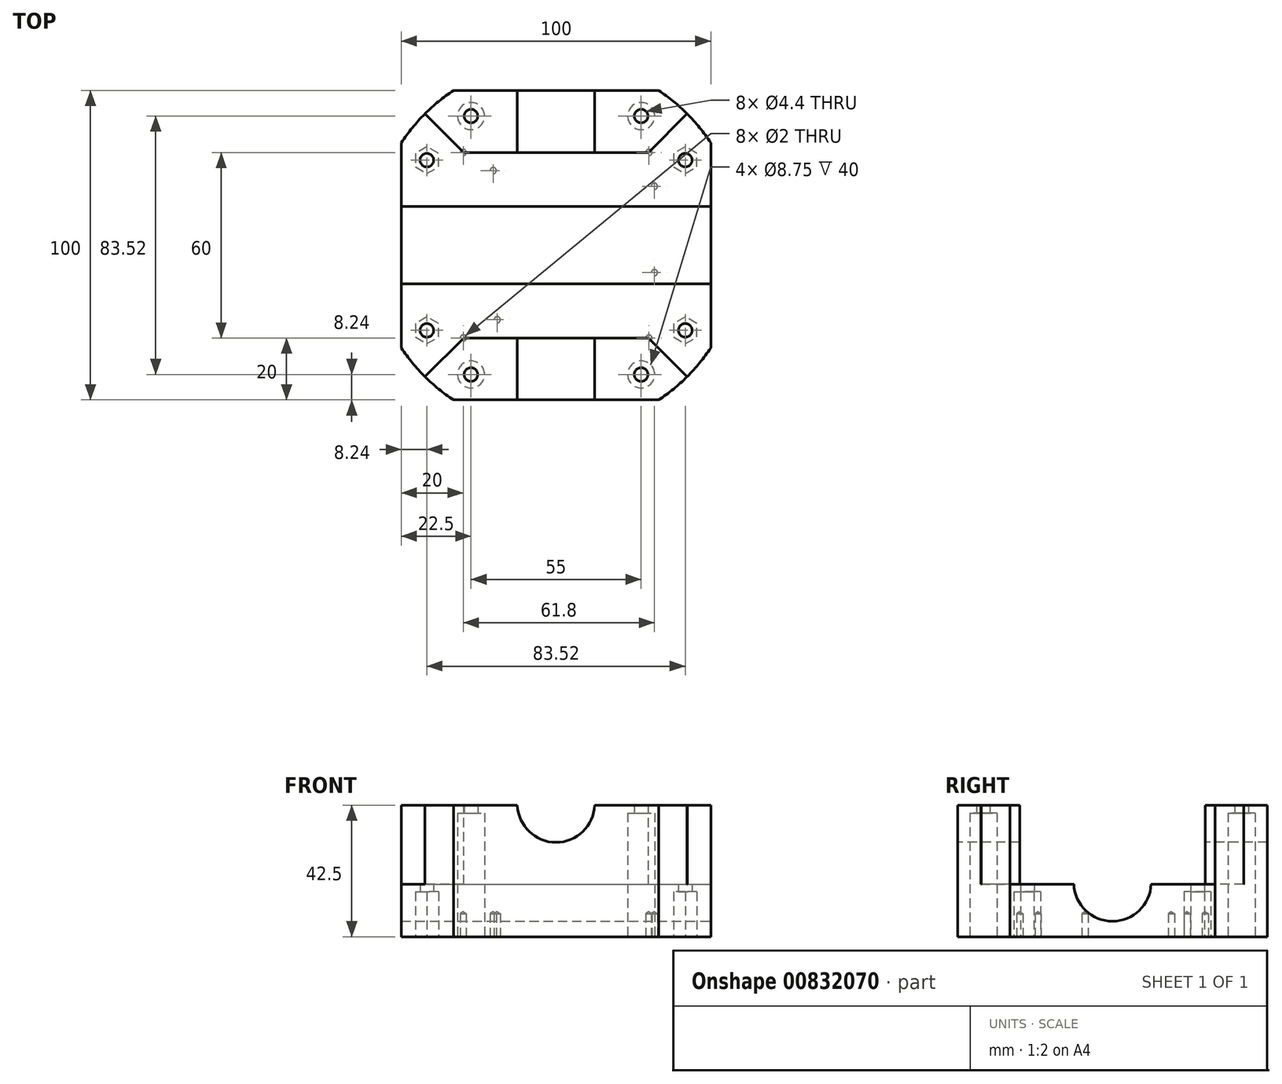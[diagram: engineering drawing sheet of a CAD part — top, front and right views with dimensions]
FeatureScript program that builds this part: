
annotation { "Feature Type Name" : "Feature", "Feature Type Description" : "" }
export const myFeature = defineFeature(function(context is Context, id is Id, definition is map)
    precondition{}
    {
        {
            var Q0;
            Q0=qCreatedBy(makeId("Top.planeOp"),FACE);
            var sketch = newSketch(context, id + "F0", { "sketchPlane" : qUnion([Q0])});
            skLineSegment(sketch, "E0.bottom", {"start": v(-33.17, 50) * mm, "end": v(33.17, 50) * mm});
            skLineSegment(sketch, "E0.top", {"start": v(-33.17, -50) * mm, "end": v(33.17, -50) * mm});
            skLineSegment(sketch, "E0.left", {"start": v(-50, 33.17) * mm, "end": v(-50, -33.17) * mm});
            skLineSegment(sketch, "E0.right", {"start": v(50, 33.17) * mm, "end": v(50, -33.17) * mm});
            skArc(sketch, "E1", {"start": v(-50, -33.17) * mm, "mid": v(-42.43, -42.43) * mm, "end": v(-33.17, -50) * mm});
            skArc(sketch, "E2.trimOffspring", {"start": v(33.17, -50) * mm, "mid": v(42.43, -42.43) * mm, "end": v(50, -33.17) * mm});
            skArc(sketch, "E3.trimOffspring", {"start": v(50, 33.17) * mm, "mid": v(42.43, 42.43) * mm, "end": v(33.17, 50) * mm});
            skArc(sketch, "E4.trimOffspring", {"start": v(-33.17, 50) * mm, "mid": v(-42.43, 42.43) * mm, "end": v(-50, 33.17) * mm});
            skSolve(sketch);
        }
        {
            var Q0;
            Q0=makeQuery(id+"F0.imprint","IMPRINT",FACE,{"disambiguationData":[TD([[makeQuery(id+"F0.imprint","IMPRINT",EDGE,{"derivedFrom":sQuery(id+"F0.wireOp",EDGE,"E0.bottom")}),-1.0]])]});
            extrude(context, id + "F1", {"entities" : qUnion([Q0]), "depth" : (17.5 + 25) * mm, "offsetDistance" : 25 * mm});
        }
        {
            var Q0;
            Q0=makeQuery(id+"F1.opExtrude","CAP_FACE",FACE,{"disambiguationData":[OSD([sQuery(id+"F0.wireOp",EDGE,"E0.bottom"),sQuery(id+"F0.wireOp",EDGE,"E0.top"),sQuery(id+"F0.wireOp",EDGE,"E0.left"),sQuery(id+"F0.wireOp",EDGE,"E0.right"),sQuery(id+"F0.wireOp",EDGE,"E1"),sQuery(id+"F0.wireOp",EDGE,"E2.trimOffspring"),sQuery(id+"F0.wireOp",EDGE,"E3.trimOffspring"),sQuery(id+"F0.wireOp",EDGE,"E4.trimOffspring")])],"isStart":false});
            var sketch = newSketch(context, id + "F2", { "sketchPlane" : qUnion([Q0])});
            skLineSegment(sketch, "E5", {"start": v(-42.43, 42.43) * mm, "end": v(-30, 30) * mm, "construction": true});
            skLineSegment(sketch, "E6", {"start": v(42.43, 42.43) * mm, "end": v(30, 30) * mm, "construction": true});
            skLineSegment(sketch, "E7.bottom", {"start": v(-30, 30) * mm, "end": v(-29.86, 30) * mm, "construction": true});
            skLineSegment(sketch, "E7.top", {"start": v(-30, -30) * mm, "end": v(-29.86, -30) * mm, "construction": true});
            skLineSegment(sketch, "E8.trimOffspring", {"start": v(30, -30) * mm, "end": v(42.43, -42.43) * mm, "construction": true});
            skLineSegment(sketch, "E9.trimOffspring", {"start": v(-30, -30) * mm, "end": v(-42.43, -42.43) * mm, "construction": true});
            skArc(sketch, "E10.0", {"start": v(-33.17, 50) * mm, "mid": v(-42.43, 42.43) * mm, "end": v(-50, 33.17) * mm});
            skArc(sketch, "E11.0.0", {"start": v(-50, -33.17) * mm, "mid": v(-42.43, -42.43) * mm, "end": v(-33.17, -50) * mm});
            skLineSegment(sketch, "E11.0.1", {"start": v(-33.17, -50) * mm, "end": v(33.17, -50) * mm});
            skArc(sketch, "E11.0.2", {"start": v(33.17, -50) * mm, "mid": v(42.43, -42.43) * mm, "end": v(50, -33.17) * mm});
            skLineSegment(sketch, "E11.0.3", {"start": v(50, -33.17) * mm, "end": v(50, 33.17) * mm});
            skArc(sketch, "E11.0.4", {"start": v(50, 33.17) * mm, "mid": v(42.43, 42.43) * mm, "end": v(33.17, 50) * mm});
            skLineSegment(sketch, "E11.0.5", {"start": v(33.17, 50) * mm, "end": v(-33.17, 50) * mm});
            skArc(sketch, "E11.0.6", {"start": v(-42.43, 42.43) * mm, "mid": v(-46.44, 37.99) * mm, "end": v(-50, 33.17) * mm});
            skLineSegment(sketch, "E11.0.7", {"start": v(-50, 33.17) * mm, "end": v(-50, -33.17) * mm});
            skArc(sketch, "E12.0.2", {"start": v(42.43, -42.43) * mm, "mid": v(46.44, -37.99) * mm, "end": v(50, -33.17) * mm});
            skArc(sketch, "E12.0.4", {"start": v(50, 33.17) * mm, "mid": v(46.44, 37.99) * mm, "end": v(42.43, 42.43) * mm});
            skLineSegment(sketch, "E13.0", {"start": v(-42.36, 42.5) * mm, "end": v(-29.86, 30) * mm});
            skLineSegment(sketch, "E14.0", {"start": v(42.36, 42.5) * mm, "end": v(29.86, 30) * mm});
            skLineSegment(sketch, "E15.0", {"start": v(29.86, -30) * mm, "end": v(42.36, -42.5) * mm});
            skLineSegment(sketch, "E16.0", {"start": v(-29.86, -30) * mm, "end": v(-42.36, -42.5) * mm});
            skLineSegment(sketch, "E17", {"start": v(-29.86, -30) * mm, "end": v(29.86, -30) * mm});
            skLineSegment(sketch, "E18", {"start": v(29.86, -30) * mm, "end": v(30, -30) * mm, "construction": true});
            skLineSegment(sketch, "E19", {"start": v(29.86, 30) * mm, "end": v(29.86, 30) * mm});
            skLineSegment(sketch, "E20", {"start": v(-29.86, 30) * mm, "end": v(29.86, 30) * mm});
            skLineSegment(sketch, "E21", {"start": v(29.86, 30) * mm, "end": v(30, 30) * mm, "construction": true});
            skSolve(sketch);
        }
        {
            var Q0;
            {var subQ2=sQuery(id+"F2.wireOp",EDGE,"E12.0.2");Q0=makeQuery(id+"F2.imprint","IMPRINT",FACE,{"disambiguationData":[TD([[makeQuery(id+"F2.imprint","IMPRINT",EDGE,{"derivedFrom":subQ2}),1.0]])]});}
            extrude(context, id + "F3", {"entities" : qUnion([Q0]), "operationType" : NewBodyOperationType.REMOVE, "flatOperationType" : FlatOperationType.REMOVE, "oppositeDirection" : true, "depth" : 25.5 * mm, "offsetDistance" : 25 * mm, "domain" : OperationDomain.MODEL});
        }
        {
            var Q0;
            Q0=makeQuery(id+"F1.opExtrude","SWEPT_FACE",FACE,{"disambiguationData":[OSD([sQuery(id+"F0.wireOp",EDGE,"E0.top")])]});
            var sketch = newSketch(context, id + "F4", { "sketchPlane" : qUnion([Q0])});
            skCircle(sketch, "E22", {"center": v(0, 43) * mm, "radius": 12.5 * mm});
            skPoint(sketch, "E22.centerSnap0", {"position": v(0, 42.5) * mm});
            skSolve(sketch);
        }
        {
            var Q0;
            Q0 = qSketchRegion(id + "F4", true);
            extrude(context, id + "F5", {"entities" : qUnion([Q0]), "operationType" : NewBodyOperationType.REMOVE, "flatOperationType" : FlatOperationType.REMOVE, "endBound" : BoundingType.THROUGH_ALL, "oppositeDirection" : true, "depth" : 25 * mm, "offsetDistance" : 25 * mm, "domain" : OperationDomain.MODEL});
        }
        {
            var Q0;
            Q0=makeQuery(id+"F1.opExtrude","SWEPT_FACE",FACE,{"disambiguationData":[OSD([sQuery(id+"F0.wireOp",EDGE,"E0.right")])]});
            var sketch = newSketch(context, id + "F6", { "sketchPlane" : qUnion([Q0])});
            skCircle(sketch, "E23", {"center": v(0, 17.5) * mm, "radius": 12.5 * mm});
            skSolve(sketch);
        }
        {
            var Q0;
            Q0 = qSketchRegion(id + "F6", true);
            extrude(context, id + "F7", {"entities" : qUnion([Q0]), "operationType" : NewBodyOperationType.REMOVE, "endBound" : BoundingType.THROUGH_ALL, "oppositeDirection" : true, "depth" : 25 * mm, "offsetDistance" : 25 * mm});
        }
        {
            var Q0;
            Q0=makeQuery(id+"F1.opExtrude","CAP_FACE",FACE,{"disambiguationData":[OSD([sQuery(id+"F0.wireOp",EDGE,"E0.bottom"),sQuery(id+"F0.wireOp",EDGE,"E0.top"),sQuery(id+"F0.wireOp",EDGE,"E0.left"),sQuery(id+"F0.wireOp",EDGE,"E0.right"),sQuery(id+"F0.wireOp",EDGE,"E1"),sQuery(id+"F0.wireOp",EDGE,"E2.trimOffspring"),sQuery(id+"F0.wireOp",EDGE,"E3.trimOffspring"),sQuery(id+"F0.wireOp",EDGE,"E4.trimOffspring")])],"isStart":true});
            var sketch = newSketch(context, id + "F8", { "sketchPlane" : qUnion([Q0])});
            skLineSegment(sketch, "E24", {"start": v(-42.43, 42.43) * mm, "end": v(42.43, -42.43) * mm, "construction": true});
            skLineSegment(sketch, "E25", {"start": v(42.43, 42.43) * mm, "end": v(-42.43, -42.43) * mm, "construction": true});
            skCircle(sketch, "E26", {"center": v(0, 0) * mm, "radius": 50 * mm, "construction": true});
            skPoint(sketch, "E27", {"position": v(-27.5, 41.76) * mm});
            skPoint(sketch, "E28", {"position": v(27.5, 41.76) * mm});
            skPoint(sketch, "E29", {"position": v(27.5, -41.76) * mm});
            skPoint(sketch, "E30", {"position": v(-27.5, -41.76) * mm});
            skPoint(sketch, "E31", {"position": v(-41.76, 27.5) * mm});
            skPoint(sketch, "E32", {"position": v(-41.76, -27.5) * mm});
            skPoint(sketch, "E33", {"position": v(41.76, -27.5) * mm});
            skPoint(sketch, "E34", {"position": v(41.76, 27.5) * mm});
            skSolve(sketch);
        }
        {
            var Q0;
            Q0=sQuery(id+"F8.wireOp",VERTEX,"E27");
            var Q1;
            Q1=sQuery(id+"F8.wireOp",VERTEX,"E28");
            var Q2;
            Q2=sQuery(id+"F8.wireOp",VERTEX,"E29");
            var Q3;
            Q3=sQuery(id+"F8.wireOp",VERTEX,"E30");
            var Q4;
            Q4=makeQuery(id+"F1.opExtrude","SWEPT_BODY",BODY,{"disambiguationData":[OSD([sQuery(id+"F0.wireOp",EDGE,"E0.bottom"),sQuery(id+"F0.wireOp",EDGE,"E0.top"),sQuery(id+"F0.wireOp",EDGE,"E0.left"),sQuery(id+"F0.wireOp",EDGE,"E0.right"),sQuery(id+"F0.wireOp",EDGE,"E1"),sQuery(id+"F0.wireOp",EDGE,"E2.trimOffspring"),sQuery(id+"F0.wireOp",EDGE,"E3.trimOffspring"),sQuery(id+"F0.wireOp",EDGE,"E4.trimOffspring")])]});
            hole(context, id + "F9", {"style" : HoleStyle.C_BORE, "endStyle" : HoleEndStyle.THROUGH, "holeDiameter" : 4.4 * mm, "cBoreDiameter" : 8.75 * mm, "cBoreDepth" : 40 * mm, "majorDiameter" : 5 * mm, "isTappedThrough" : true, "tappedDepth" : 12 * mm, "tapClearance" : 3, "locations" : qUnion([Q0, Q1, Q2, Q3]), "scope" : qUnion([Q4])});
        }
        {
            var Q0;
            Q0=sQuery(id+"F8.wireOp",VERTEX,"E31");
            var Q1;
            Q1=sQuery(id+"F8.wireOp",VERTEX,"E32");
            var Q2;
            Q2=sQuery(id+"F8.wireOp",VERTEX,"E33");
            var Q3;
            Q3=sQuery(id+"F8.wireOp",VERTEX,"E34");
            var Q4;
            Q4=makeQuery(id+"F1.opExtrude","SWEPT_BODY",BODY,{"disambiguationData":[OSD([sQuery(id+"F0.wireOp",EDGE,"E0.bottom"),sQuery(id+"F0.wireOp",EDGE,"E0.top"),sQuery(id+"F0.wireOp",EDGE,"E0.left"),sQuery(id+"F0.wireOp",EDGE,"E0.right"),sQuery(id+"F0.wireOp",EDGE,"E1"),sQuery(id+"F0.wireOp",EDGE,"E2.trimOffspring"),sQuery(id+"F0.wireOp",EDGE,"E3.trimOffspring"),sQuery(id+"F0.wireOp",EDGE,"E4.trimOffspring")])]});
            hole(context, id + "F10", {"style" : HoleStyle.SIMPLE, "endStyle" : HoleEndStyle.THROUGH, "standardTappedOrClearance" : lookupTablePath({ "fit" : "Normal", "standard" : "ISO", "size" : "M4", "type" : "Clearance" }), "standardBlindInLast" : lookupTablePath({ "fit" : "Standard", "standard" : "ISO", "size" : "M4", "type" : "Clearance" }), "holeDiameter" : 4.4 * mm, "majorDiameter" : 5 * mm, "isTappedThrough" : true, "tappedDepth" : 12 * mm, "tapClearance" : 3, "locations" : qUnion([Q0, Q1, Q2, Q3]), "scope" : qUnion([Q4])});
        }
        {
            var Q0;
            Q0=makeQuery(id+"F1.opExtrude","CAP_FACE",FACE,{"disambiguationData":[OSD([sQuery(id+"F0.wireOp",EDGE,"E0.bottom"),sQuery(id+"F0.wireOp",EDGE,"E0.top"),sQuery(id+"F0.wireOp",EDGE,"E0.left"),sQuery(id+"F0.wireOp",EDGE,"E0.right"),sQuery(id+"F0.wireOp",EDGE,"E1"),sQuery(id+"F0.wireOp",EDGE,"E2.trimOffspring"),sQuery(id+"F0.wireOp",EDGE,"E3.trimOffspring"),sQuery(id+"F0.wireOp",EDGE,"E4.trimOffspring")])],"isStart":true});
            var sketch = newSketch(context, id + "F11", { "sketchPlane" : qUnion([Q0])});
            skCircle(sketch, "E35.cCircle", {"center": v(-41.76, 27.5) * mm, "radius": 4.33 * mm, "construction": true});
            skLineSegment(sketch, "E35.0", {"start": v(-38, 25.33) * mm, "end": v(-41.76, 23.17) * mm});
            skLineSegment(sketch, "E35.1", {"start": v(-41.76, 23.17) * mm, "end": v(-45.5, 25.33) * mm});
            skLineSegment(sketch, "E35.2", {"start": v(-45.5, 25.33) * mm, "end": v(-45.5, 29.67) * mm});
            skLineSegment(sketch, "E35.3", {"start": v(-45.5, 29.67) * mm, "end": v(-41.76, 31.83) * mm});
            skLineSegment(sketch, "E35.4", {"start": v(-41.76, 31.83) * mm, "end": v(-38, 29.67) * mm});
            skLineSegment(sketch, "E35.5", {"start": v(-38, 29.67) * mm, "end": v(-38, 25.33) * mm});
            skCircle(sketch, "E36.cCircle", {"center": v(-41.76, -27.5) * mm, "radius": 4.33 * mm, "construction": true});
            skLineSegment(sketch, "E36.0", {"start": v(-38, -29.67) * mm, "end": v(-41.76, -31.83) * mm});
            skLineSegment(sketch, "E36.1", {"start": v(-41.76, -31.83) * mm, "end": v(-45.5, -29.67) * mm});
            skLineSegment(sketch, "E36.2", {"start": v(-45.5, -29.67) * mm, "end": v(-45.5, -25.33) * mm});
            skLineSegment(sketch, "E36.3", {"start": v(-45.5, -25.33) * mm, "end": v(-41.76, -23.17) * mm});
            skLineSegment(sketch, "E36.4", {"start": v(-41.76, -23.17) * mm, "end": v(-38, -25.33) * mm});
            skLineSegment(sketch, "E36.5", {"start": v(-38, -25.33) * mm, "end": v(-38, -29.67) * mm});
            skCircle(sketch, "E37.cCircle", {"center": v(41.76, -27.5) * mm, "radius": 4.33 * mm, "construction": true});
            skLineSegment(sketch, "E37.0", {"start": v(38, -25.33) * mm, "end": v(41.76, -23.17) * mm});
            skLineSegment(sketch, "E37.1", {"start": v(41.76, -23.17) * mm, "end": v(45.5, -25.33) * mm});
            skLineSegment(sketch, "E37.2", {"start": v(45.5, -25.33) * mm, "end": v(45.5, -29.67) * mm});
            skLineSegment(sketch, "E37.3", {"start": v(45.5, -29.67) * mm, "end": v(41.76, -31.83) * mm});
            skLineSegment(sketch, "E37.4", {"start": v(41.76, -31.83) * mm, "end": v(38, -29.67) * mm});
            skLineSegment(sketch, "E37.5", {"start": v(38, -29.67) * mm, "end": v(38, -25.33) * mm});
            skCircle(sketch, "E38.cCircle", {"center": v(41.76, 27.5) * mm, "radius": 4.33 * mm, "construction": true});
            skLineSegment(sketch, "E38.0", {"start": v(38, 25.33) * mm, "end": v(38, 29.67) * mm});
            skLineSegment(sketch, "E38.1", {"start": v(38, 29.67) * mm, "end": v(41.76, 31.83) * mm});
            skLineSegment(sketch, "E38.2", {"start": v(41.76, 31.83) * mm, "end": v(45.5, 29.67) * mm});
            skLineSegment(sketch, "E38.3", {"start": v(45.5, 29.67) * mm, "end": v(45.5, 25.33) * mm});
            skLineSegment(sketch, "E38.4", {"start": v(45.5, 25.33) * mm, "end": v(41.76, 23.17) * mm});
            skLineSegment(sketch, "E38.5", {"start": v(41.76, 23.17) * mm, "end": v(38, 25.33) * mm});
            skSolve(sketch);
        }
        {
            var Q0;
            Q0=makeQuery(id+"F11.imprint","IMPRINT",FACE,{"disambiguationData":[TD([[makeQuery(id+"F11.imprint","IMPRINT",EDGE,{"derivedFrom":sQuery(id+"F11.wireOp",EDGE,"E35.0")}),-1.0]])]});
            var Q1;
            Q1=makeQuery(id+"F11.imprint","IMPRINT",FACE,{"disambiguationData":[TD([[makeQuery(id+"F11.imprint","IMPRINT",EDGE,{"derivedFrom":sQuery(id+"F11.wireOp",EDGE,"E38.0")}),-1.0]])]});
            var Q2;
            Q2=makeQuery(id+"F11.imprint","IMPRINT",FACE,{"disambiguationData":[TD([[makeQuery(id+"F11.imprint","IMPRINT",EDGE,{"derivedFrom":sQuery(id+"F11.wireOp",EDGE,"E37.0")}),-1.0]])]});
            var Q3;
            Q3=makeQuery(id+"F11.imprint","IMPRINT",FACE,{"disambiguationData":[TD([[makeQuery(id+"F11.imprint","IMPRINT",EDGE,{"derivedFrom":sQuery(id+"F11.wireOp",EDGE,"E36.0")}),-1.0]])]});
            extrude(context, id + "F12", {"entities" : qUnion([Q0, Q1, Q2, Q3]), "operationType" : NewBodyOperationType.REMOVE, "oppositeDirection" : true, "depth" : 14.5 * mm, "offsetDistance" : 25 * mm});
        }
        {
            var Q0;
            Q0=makeQuery(id+"F1.opExtrude","CAP_FACE",FACE,{"disambiguationData":[OSD([sQuery(id+"F0.wireOp",EDGE,"E0.bottom"),sQuery(id+"F0.wireOp",EDGE,"E0.top"),sQuery(id+"F0.wireOp",EDGE,"E0.left"),sQuery(id+"F0.wireOp",EDGE,"E0.right"),sQuery(id+"F0.wireOp",EDGE,"E1"),sQuery(id+"F0.wireOp",EDGE,"E2.trimOffspring"),sQuery(id+"F0.wireOp",EDGE,"E3.trimOffspring"),sQuery(id+"F0.wireOp",EDGE,"E4.trimOffspring")])],"isStart":true});
            var sketch = newSketch(context, id + "F13", { "sketchPlane" : qUnion([Q0])});
            skLineSegment(sketch, "E39.bottom", {"start": v(-34.3, 26.65) * mm, "end": v(34.3, 26.65) * mm, "construction": true});
            skLineSegment(sketch, "E39.top", {"start": v(-34.3, -26.65) * mm, "end": v(34.3, -26.65) * mm, "construction": true});
            skLineSegment(sketch, "E39.left", {"start": v(-34.3, 26.65) * mm, "end": v(-34.3, -26.65) * mm, "construction": true});
            skLineSegment(sketch, "E39.right", {"start": v(34.3, 26.65) * mm, "end": v(34.3, -26.65) * mm, "construction": true});
            skLineSegment(sketch, "E40", {"start": v(-34.3, 26.65) * mm, "end": v(34.3, -26.65) * mm, "construction": true});
            skPoint(sketch, "E41", {"position": v(-19, 24.05) * mm});
            skPoint(sketch, "E42", {"position": v(31.8, 8.85) * mm});
            skPoint(sketch, "E43", {"position": v(31.8, -19.05) * mm});
            skPoint(sketch, "E44", {"position": v(-20.3, -24.15) * mm});
            skSolve(sketch);
        }
        {
            var Q0;
            Q0=makeQuery(id+"F13.imprint","IMPRINT",FACE,{"disambiguationData":[TD([[makeQuery(id+"F13.imprint","IMPRINT",EDGE,{"derivedFrom":makeQuery(id+"F1.opExtrude","CAP_EDGE",EDGE,{"disambiguationData":[OSD([sQuery(id+"F0.wireOp",EDGE,"E0.bottom")])],"isStart":true})}),1.0]])]});
            var sketch = newSketch(context, id + "F14", { "sketchPlane" : qUnion([Q0])});
            skPoint(sketch, "E45", {"position": v(-30, 30) * mm});
            skPoint(sketch, "E46", {"position": v(30, 30) * mm});
            skPoint(sketch, "E47", {"position": v(30, -30) * mm});
            skPoint(sketch, "E48", {"position": v(-30, -30) * mm});
            skLineSegment(sketch, "E49", {"start": v(-30, 30) * mm, "end": v(30, -30) * mm, "construction": true});
            skSolve(sketch);
        }
        {
            var Q0;
            Q0=sQuery(id+"F14.wireOp",VERTEX,"E45");
            var Q1;
            Q1=sQuery(id+"F14.wireOp",VERTEX,"E46");
            var Q2;
            Q2=sQuery(id+"F13.wireOp",VERTEX,"E42");
            var Q3;
            Q3=sQuery(id+"F13.wireOp",VERTEX,"E43");
            var Q4;
            Q4=sQuery(id+"F14.wireOp",VERTEX,"E47");
            var Q5;
            Q5=sQuery(id+"F13.wireOp",VERTEX,"E44");
            var Q6;
            Q6=sQuery(id+"F14.wireOp",VERTEX,"E48");
            var Q7;
            Q7=sQuery(id+"F13.wireOp",VERTEX,"E41");
            var Q8;
            Q8=makeQuery(id+"F1.opExtrude","SWEPT_BODY",BODY,{"disambiguationData":[OSD([sQuery(id+"F0.wireOp",EDGE,"E0.bottom"),sQuery(id+"F0.wireOp",EDGE,"E0.top"),sQuery(id+"F0.wireOp",EDGE,"E0.left"),sQuery(id+"F0.wireOp",EDGE,"E0.right"),sQuery(id+"F0.wireOp",EDGE,"E1"),sQuery(id+"F0.wireOp",EDGE,"E2.trimOffspring"),sQuery(id+"F0.wireOp",EDGE,"E3.trimOffspring"),sQuery(id+"F0.wireOp",EDGE,"E4.trimOffspring")])]});
            hole(context, id + "F15", {"style" : HoleStyle.SIMPLE, "endStyle" : HoleEndStyle.BLIND, "holeDiameter" : 2 * mm, "majorDiameter" : 5 * mm, "holeDepth" : 7.5 * mm, "isTappedThrough" : true, "tappedDepth" : 12 * mm, "tapClearance" : 3, "locations" : qUnion([Q0, Q1, Q2, Q3, Q4, Q5, Q6, Q7]), "scope" : qUnion([Q8])});
        }
    });
